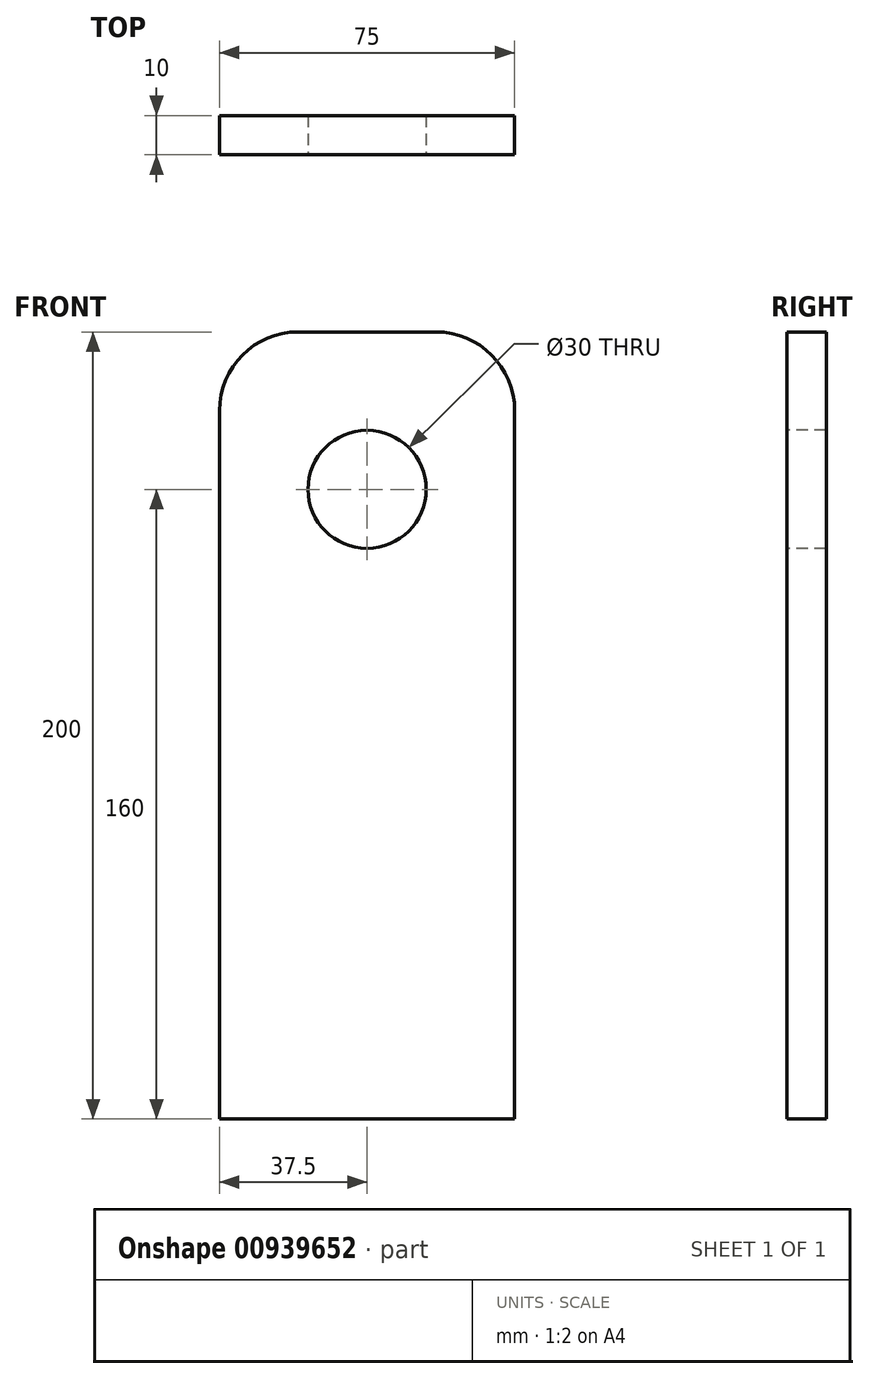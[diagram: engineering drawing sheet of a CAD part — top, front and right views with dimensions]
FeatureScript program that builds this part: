
annotation { "Feature Type Name" : "Feature", "Feature Type Description" : "" }
export const myFeature = defineFeature(function(context is Context, id is Id, definition is map)
    precondition{}
    {
        {
            var Q0;
            Q0=qCreatedBy(makeId("Front.planeOp"),FACE);
            var sketch = newSketch(context, id + "F0", { "sketchPlane" : qUnion([Q0])});
            skLineSegment(sketch, "E0.bottom", {"start": v(37.5, -100) * mm, "end": v(-37.5, -100) * mm});
            skLineSegment(sketch, "E0.top", {"start": v(37.5, 100) * mm, "end": v(-37.5, 100) * mm});
            skLineSegment(sketch, "E0.left", {"start": v(37.5, -100) * mm, "end": v(37.5, 100) * mm});
            skLineSegment(sketch, "E0.right", {"start": v(-37.5, -100) * mm, "end": v(-37.5, 100) * mm});
            skPoint(sketch, "E0.middle", {"position": v(0, 0) * mm});
            skSolve(sketch);
        }
        {
            var Q0;
            Q0 = qSketchRegion(id + "F0", true);
            extrude(context, id + "F1", {"entities" : qUnion([Q0]), "depth" : 10 * mm, "offsetDistance" : 25 * mm});
        }
        {
            var Q0;
            Q0=qCreatedBy(makeId("Front.planeOp"),FACE);
            var sketch = newSketch(context, id + "F2", { "sketchPlane" : qUnion([Q0])});
            skCircle(sketch, "E1", {"center": v(0, 60) * mm, "radius": 15 * mm});
            skSolve(sketch);
        }
        {
            var Q0;
            Q0 = qSketchRegion(id + "F2", true);
            extrude(context, id + "F3", {"entities" : qUnion([Q0]), "operationType" : NewBodyOperationType.REMOVE, "endBound" : BoundingType.THROUGH_ALL, "oppositeDirection" : true, "depth" : 25 * mm, "offsetDistance" : 25 * mm, "hasSecondDirection" : true, "secondDirectionOppositeDirection" : false, "secondDirectionDepth" : 25 * mm});
        }
        {
            var Q0;
            Q0=makeQuery(id+"F1.opExtrude","SWEPT_EDGE",EDGE,{"disambiguationData":[OSD([sQuery(id+"F0.wireOp",EDGE,"E0.top"),sQuery(id+"F0.wireOp",EDGE,"E0.right")])]});
            var Q1;
            Q1=makeQuery(id+"F1.opExtrude","SWEPT_EDGE",EDGE,{"disambiguationData":[OSD([sQuery(id+"F0.wireOp",EDGE,"E0.top"),sQuery(id+"F0.wireOp",EDGE,"E0.left")])]});
            fillet(context, id + "F4", {"entities" : qUnion([Q0, Q1]), "radius" : 20 * mm, "tangentPropagation" : true, "allowEdgeOverflow" : false});
        }
    });
